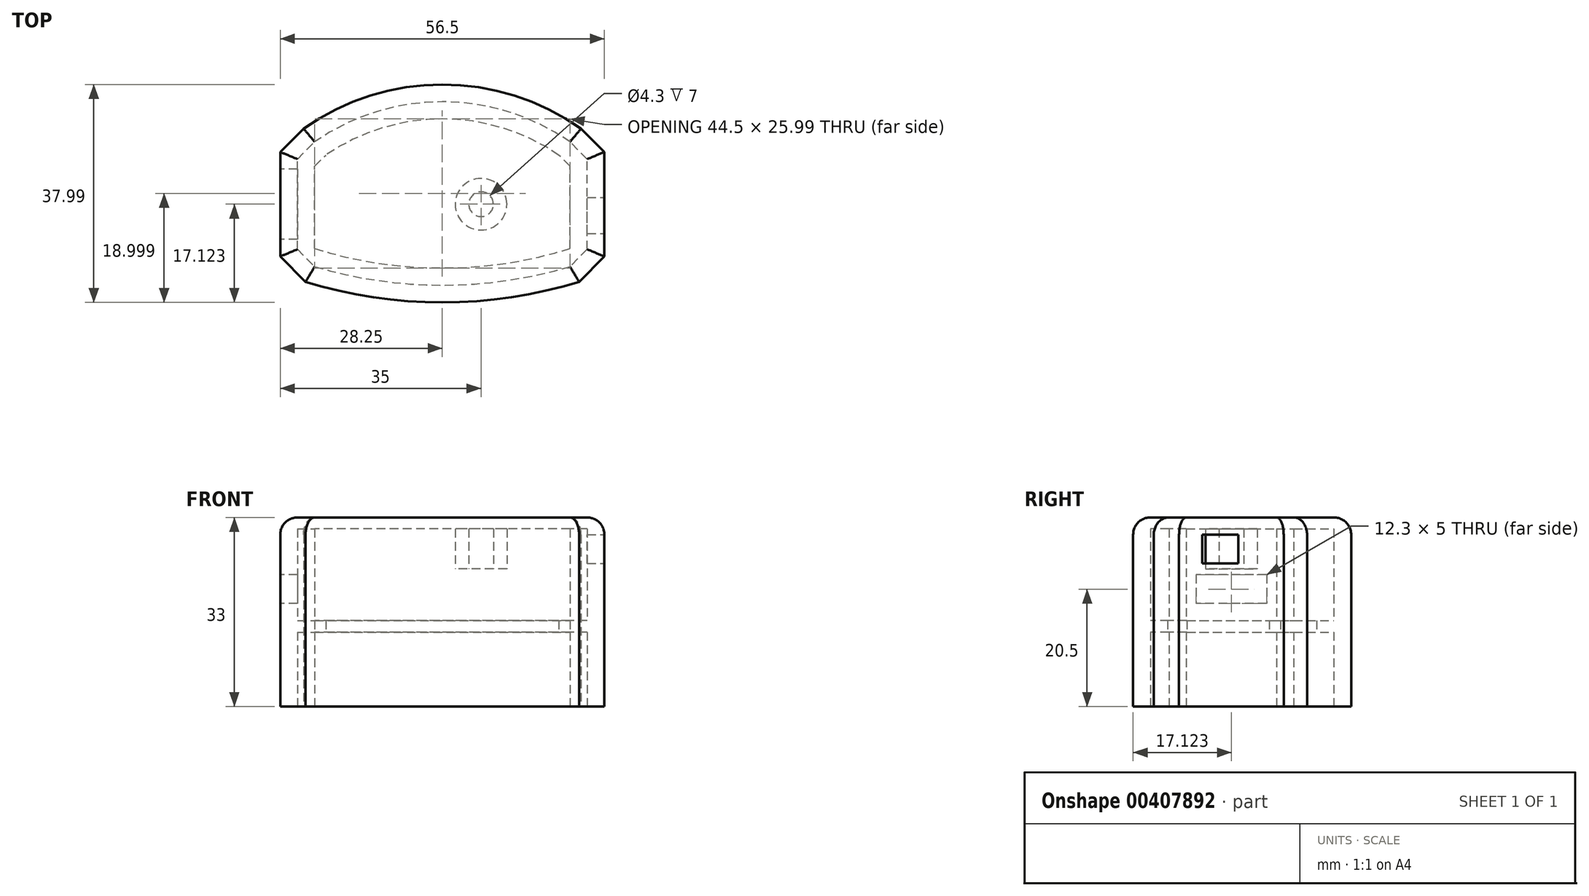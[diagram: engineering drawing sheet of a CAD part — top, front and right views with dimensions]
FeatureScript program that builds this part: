
annotation { "Feature Type Name" : "Feature", "Feature Type Description" : "" }
export const myFeature = defineFeature(function(context is Context, id is Id, definition is map)
    precondition{}
    {
        {
            var Q0;
            Q0=qCreatedBy(makeId("Top.planeOp"),FACE);
            var sketch = newSketch(context, id + "F0", { "sketchPlane" : qUnion([Q0])});
            skLineSegment(sketch, "E0.left", {"start": v(-25.25, -1.8) * mm, "end": v(-25.25, 13.94) * mm});
            skLineSegment(sketch, "E0.right", {"start": v(25.25, -1.8) * mm, "end": v(25.25, 13.94) * mm});
            skLineSegment(sketch, "E1", {"start": v(25.25, 13.94) * mm, "end": v(22.24, 16.95) * mm});
            skLineSegment(sketch, "E2", {"start": v(25.25, -1.8) * mm, "end": v(22.24, -4.8) * mm});
            skLineSegment(sketch, "E3", {"start": v(-25.25, 13.94) * mm, "end": v(-22.24, 16.95) * mm});
            skLineSegment(sketch, "E4", {"start": v(-25.25, -1.8) * mm, "end": v(-22.24, -4.8) * mm});
            skArc(sketch, "E5", {"start": v(22.24, 16.95) * mm, "mid": v(0, 23.94) * mm, "end": v(-22.24, 16.95) * mm});
            skArc(sketch, "E6", {"start": v(-22.24, -4.8) * mm, "mid": v(0, -8.05) * mm, "end": v(22.24, -4.8) * mm});
            skLineSegment(sketch, "E7", {"start": v(-25.25, -1.8) * mm, "end": v(25.25, -1.8) * mm, "construction": true});
            skLineSegment(sketch, "E8", {"start": v(-25.25, 13.94) * mm, "end": v(25.25, 13.94) * mm, "construction": true});
            skLineSegment(sketch, "E9.0", {"start": v(28.25, 15.19) * mm, "end": v(24.18, 19.25) * mm});
            skLineSegment(sketch, "E9.1", {"start": v(28.25, -3.04) * mm, "end": v(28.25, 15.19) * mm});
            skArc(sketch, "E9.2", {"start": v(24.18, 19.25) * mm, "mid": v(0, 26.94) * mm, "end": v(-24.18, 19.25) * mm});
            skLineSegment(sketch, "E9.3", {"start": v(28.25, -3.04) * mm, "end": v(23.83, -7.45) * mm});
            skLineSegment(sketch, "E9.4", {"start": v(-28.25, 15.19) * mm, "end": v(-24.18, 19.25) * mm});
            skLineSegment(sketch, "E9.5", {"start": v(-28.25, -3.04) * mm, "end": v(-28.25, 15.19) * mm});
            skLineSegment(sketch, "E9.6", {"start": v(-28.25, -3.04) * mm, "end": v(-23.83, -7.45) * mm});
            skArc(sketch, "E9.7", {"start": v(-23.83, -7.45) * mm, "mid": v(0, -11.05) * mm, "end": v(23.83, -7.45) * mm});
            skLineSegment(sketch, "E10.0", {"start": v(22.25, 12.7) * mm, "end": v(20.31, 14.64) * mm});
            skLineSegment(sketch, "E10.1", {"start": v(-22.25, 12.7) * mm, "end": v(-20.31, 14.64) * mm});
            skLineSegment(sketch, "E10.2", {"start": v(-22.25, -1.66) * mm, "end": v(-22.25, 12.7) * mm});
            skArc(sketch, "E10.3", {"start": v(20.31, 14.64) * mm, "mid": v(0, 20.94) * mm, "end": v(-20.31, 14.64) * mm});
            skArc(sketch, "E10.4", {"start": v(-22.25, -1.66) * mm, "mid": v(0, -5.05) * mm, "end": v(22.25, -1.66) * mm});
            skLineSegment(sketch, "E10.5", {"start": v(22.25, -1.66) * mm, "end": v(22.25, 12.7) * mm});
            skCircle(sketch, "E11", {"center": v(6.75, 6.07) * mm, "radius": 4.5 * mm});
            skCircle(sketch, "E12", {"center": v(6.75, 6.07) * mm, "radius": 2.15 * mm});
            skSolve(sketch);
        }
        {
            var Q0;
            Q0=makeQuery(id+"F0.imprint","IMPRINT",FACE,{"disambiguationData":[TD([[makeQuery(id+"F0.imprint","IMPRINT",EDGE,{"derivedFrom":sQuery(id+"F0.wireOp",EDGE,"E0.left")}),1.0]])]});
            var Q1;
            Q1=makeQuery(id+"F0.imprint","IMPRINT",FACE,{"disambiguationData":[TD([[makeQuery(id+"F0.imprint","IMPRINT",EDGE,{"derivedFrom":sQuery(id+"F0.wireOp",EDGE,"E0.left")}),-1.0]])]});
            var Q2;
            Q2=makeQuery(id+"F0.imprint","IMPRINT",FACE,{"disambiguationData":[TD([[makeQuery(id+"F0.imprint","IMPRINT",EDGE,{"derivedFrom":sQuery(id+"F0.wireOp",EDGE,"E10.0")}),1.0]])]});
            var Q3;
            Q3=makeQuery(id+"F0.imprint","IMPRINT",FACE,{"disambiguationData":[TD([[makeQuery(id+"F0.imprint","IMPRINT",EDGE,{"derivedFrom":sQuery(id+"F0.wireOp",EDGE,"E11")}),1.0]])]});
            var Q4;
            Q4=makeQuery(id+"F0.imprint","IMPRINT",FACE,{"disambiguationData":[TD([[makeQuery(id+"F0.imprint","IMPRINT",EDGE,{"derivedFrom":sQuery(id+"F0.wireOp",EDGE,"E12")}),1.0]])]});
            extrude(context, id + "F1", {"entities" : qUnion([Q0, Q1, Q2, Q3, Q4]), "depth" : 33 * mm});
        }
        {
            var Q0;
            Q0=makeQuery(id+"F0.imprint","IMPRINT",FACE,{"disambiguationData":[TD([[makeQuery(id+"F0.imprint","IMPRINT",EDGE,{"derivedFrom":sQuery(id+"F0.wireOp",EDGE,"E0.left")}),-1.0]])]});
            var Q1;
            Q1=makeQuery(id+"F0.imprint","IMPRINT",FACE,{"disambiguationData":[TD([[makeQuery(id+"F0.imprint","IMPRINT",EDGE,{"derivedFrom":sQuery(id+"F0.wireOp",EDGE,"E10.0")}),1.0]])]});
            extrude(context, id + "F2", {"entities" : qUnion([Q0, Q1]), "operationType" : NewBodyOperationType.REMOVE, "depth" : 31 * mm});
        }
        {
            var Q0;
            Q0=makeQuery(id+"F0.imprint","IMPRINT",FACE,{"disambiguationData":[TD([[makeQuery(id+"F0.imprint","IMPRINT",EDGE,{"derivedFrom":sQuery(id+"F0.wireOp",EDGE,"E0.left")}),-1.0]])]});
            extrude(context, id + "F3", {"entities" : qUnion([Q0]), "operationType" : NewBodyOperationType.ADD, "depth" : 15 * mm});
        }
        {
            var Q0;
            Q0=makeQuery(id+"F0.imprint","IMPRINT",FACE,{"disambiguationData":[TD([[makeQuery(id+"F0.imprint","IMPRINT",EDGE,{"derivedFrom":sQuery(id+"F0.wireOp",EDGE,"E0.left")}),-1.0]])]});
            extrude(context, id + "F4", {"entities" : qUnion([Q0]), "operationType" : NewBodyOperationType.REMOVE, "depth" : 13 * mm});
        }
        {
            var Q0;
            Q0=makeQuery(id+"F0.imprint","IMPRINT",FACE,{"disambiguationData":[TD([[makeQuery(id+"F0.imprint","IMPRINT",EDGE,{"derivedFrom":sQuery(id+"F0.wireOp",EDGE,"E12")}),1.0]])]});
            extrude(context, id + "F5", {"entities" : qUnion([Q0]), "operationType" : NewBodyOperationType.REMOVE, "depth" : 31 * mm});
        }
        {
            var Q0;
            Q0=makeQuery(id+"F1.opExtrude","CAP_EDGE",EDGE,{"disambiguationData":[OSD([sQuery(id+"F0.wireOp",EDGE,"E9.7")])],"isStart":false});
            var Q1;
            Q1=makeQuery(id+"F1.opExtrude","CAP_EDGE",EDGE,{"disambiguationData":[OSD([sQuery(id+"F0.wireOp",EDGE,"E9.5")])],"isStart":false});
            var Q2;
            Q2=makeQuery(id+"F1.opExtrude","CAP_EDGE",EDGE,{"disambiguationData":[OSD([sQuery(id+"F0.wireOp",EDGE,"E9.2")])],"isStart":false});
            var Q3;
            Q3=makeQuery(id+"F1.opExtrude","CAP_EDGE",EDGE,{"disambiguationData":[OSD([sQuery(id+"F0.wireOp",EDGE,"E9.1")])],"isStart":false});
            var Q4;
            Q4=makeQuery(id+"F1.opExtrude","CAP_EDGE",EDGE,{"disambiguationData":[OSD([sQuery(id+"F0.wireOp",EDGE,"E9.6")])],"isStart":false});
            var Q5;
            Q5=makeQuery(id+"F1.opExtrude","CAP_EDGE",EDGE,{"disambiguationData":[OSD([sQuery(id+"F0.wireOp",EDGE,"E9.3")])],"isStart":false});
            var Q6;
            Q6=makeQuery(id+"F1.opExtrude","CAP_EDGE",EDGE,{"disambiguationData":[OSD([sQuery(id+"F0.wireOp",EDGE,"E9.0")])],"isStart":false});
            var Q7;
            Q7=makeQuery(id+"F1.opExtrude","CAP_EDGE",EDGE,{"disambiguationData":[OSD([sQuery(id+"F0.wireOp",EDGE,"E9.4")])],"isStart":false});
            fillet(context, id + "F6", {"entities" : qUnion([Q0, Q1, Q2, Q3, Q4, Q5, Q6, Q7]), "radius" : 3 * mm, "tangentPropagation" : true, "allowEdgeOverflow" : false});
        }
        {
            var Q0;
            Q0=makeQuery(id+"F0.imprint","IMPRINT",FACE,{"disambiguationData":[TD([[makeQuery(id+"F0.imprint","IMPRINT",EDGE,{"derivedFrom":sQuery(id+"F0.wireOp",EDGE,"E11")}),1.0]])]});
            var Q1;
            Q1=makeQuery(id+"F0.imprint","IMPRINT",FACE,{"disambiguationData":[TD([[makeQuery(id+"F0.imprint","IMPRINT",EDGE,{"derivedFrom":sQuery(id+"F0.wireOp",EDGE,"E12")}),1.0]])]});
            extrude(context, id + "F7", {"entities" : qUnion([Q0, Q1]), "operationType" : NewBodyOperationType.REMOVE, "depth" : 24 * mm, "offsetDistance" : 25 * mm});
        }
        {
            var Q0;
            Q0=makeQuery(id+"F1.opExtrude","SWEPT_FACE",FACE,{"disambiguationData":[OSD([sQuery(id+"F0.wireOp",EDGE,"E9.1")])]});
            var sketch = newSketch(context, id + "F8", { "sketchPlane" : qUnion([Q0])});
            skLineSegment(sketch, "E13.bottom", {"start": v(7.26, 30) * mm, "end": v(0.96, 30) * mm});
            skLineSegment(sketch, "E13.top", {"start": v(7.26, 25) * mm, "end": v(0.96, 25) * mm});
            skLineSegment(sketch, "E13.left", {"start": v(7.26, 30) * mm, "end": v(7.26, 25) * mm});
            skLineSegment(sketch, "E13.right", {"start": v(0.96, 30) * mm, "end": v(0.96, 25) * mm});
            skSolve(sketch);
        }
        {
            var Q0;
            Q0=makeQuery(id+"F8.imprint","IMPRINT",FACE,{"disambiguationData":[TD([[makeQuery(id+"F8.imprint","IMPRINT",EDGE,{"derivedFrom":sQuery(id+"F8.wireOp",EDGE,"E13.bottom")}),1.0]])]});
            extrude(context, id + "F9", {"entities" : qUnion([Q0]), "operationType" : NewBodyOperationType.REMOVE, "oppositeDirection" : true, "depth" : 4 * mm, "offsetDistance" : 25 * mm});
        }
        {
            var Q0;
            Q0=makeQuery(id+"F1.opExtrude","SWEPT_FACE",FACE,{"disambiguationData":[OSD([sQuery(id+"F0.wireOp",EDGE,"E9.5")])]});
            var sketch = newSketch(context, id + "F10", { "sketchPlane" : qUnion([Q0])});
            skLineSegment(sketch, "E14.bottom", {"start": v(-12.22, 23) * mm, "end": v(0.08, 23) * mm});
            skLineSegment(sketch, "E14.top", {"start": v(-12.22, 18) * mm, "end": v(0.08, 18) * mm});
            skLineSegment(sketch, "E14.left", {"start": v(-12.22, 23) * mm, "end": v(-12.22, 18) * mm});
            skLineSegment(sketch, "E14.right", {"start": v(0.08, 23) * mm, "end": v(0.08, 18) * mm});
            skSolve(sketch);
        }
        {
            var Q0;
            Q0=makeQuery(id+"F10.imprint","IMPRINT",FACE,{"disambiguationData":[TD([[makeQuery(id+"F10.imprint","IMPRINT",EDGE,{"derivedFrom":sQuery(id+"F10.wireOp",EDGE,"E14.bottom")}),-1.0]])]});
            extrude(context, id + "F11", {"entities" : qUnion([Q0]), "operationType" : NewBodyOperationType.REMOVE, "oppositeDirection" : true, "depth" : 4 * mm, "offsetDistance" : 25 * mm});
        }
    });
